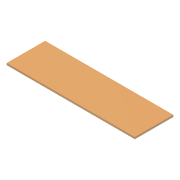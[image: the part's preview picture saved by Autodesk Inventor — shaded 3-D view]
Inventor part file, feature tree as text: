
AUTODESK INVENTOR PART (.ipt)
format: ipt  version: 2014 (Build 180170000, 170)  size: 78,848 bytes
history: native  units: mm
features: extrude x1, sketch x1
ambient origin geometry x8: Origin, YZ Plane, XZ Plane, XY Plane, X Axis, Y Axis, Z Axis, Center Point
bodies: Solid1 (feature_tree)
feature tree (2):
  extrude  "Extrusion1"  Depth=200.0mm
  sketch  "Sketch1"  dims[d0=60.0mm d1=200.0mm d2=3.0mm d3=0.0mm]
